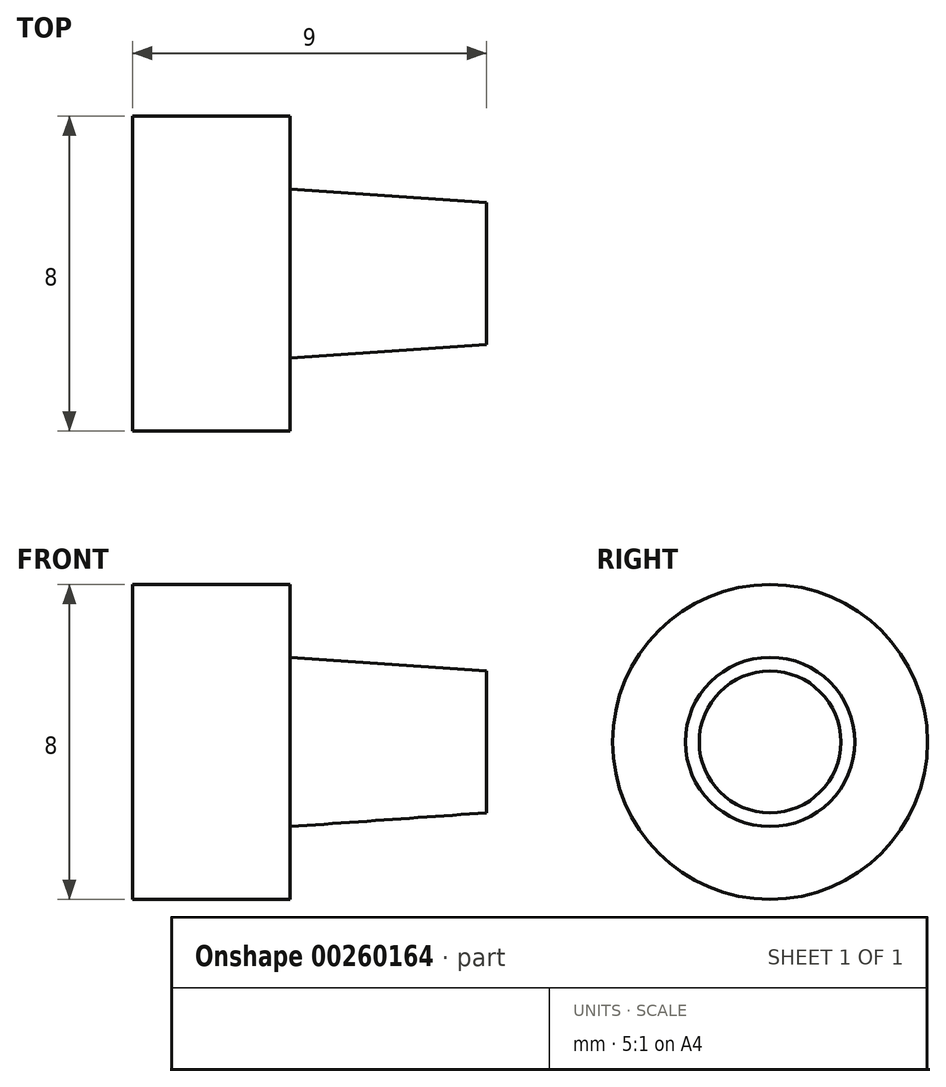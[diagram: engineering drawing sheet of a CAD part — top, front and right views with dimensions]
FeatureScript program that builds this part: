
annotation { "Feature Type Name" : "Feature", "Feature Type Description" : "" }
export const myFeature = defineFeature(function(context is Context, id is Id, definition is map)
    precondition{}
    {
        {
            var Q0;
            Q0=qCreatedBy(makeId("Front.planeOp"),FACE);
            var sketch = newSketch(context, id + "F0", { "sketchPlane" : qUnion([Q0])});
            skLineSegment(sketch, "E0", {"start": v(0, 0) * mm, "end": v(0, 4) * mm});
            skLineSegment(sketch, "E1", {"start": v(0, 4) * mm, "end": v(4, 4) * mm});
            skLineSegment(sketch, "E2", {"start": v(4, 4) * mm, "end": v(4, 2.15) * mm});
            skLineSegment(sketch, "E3", {"start": v(4, 2.15) * mm, "end": v(9, 1.8) * mm});
            skLineSegment(sketch, "E4", {"start": v(9, 1.8) * mm, "end": v(9, 0) * mm});
            skLineSegment(sketch, "E5", {"start": v(9, 0) * mm, "end": v(0, 0) * mm});
            skSolve(sketch);
        }
        {
            var Q0;
            Q0=makeQuery(id+"F0.imprint","IMPRINT",FACE,{"disambiguationData":[TD([[makeQuery(id+"F0.imprint","IMPRINT",EDGE,{"derivedFrom":sQuery(id+"F0.wireOp",EDGE,"E0")}),-1.0]])]});
            var Q1;
            Q1=sQuery(id+"F0.wireOp",EDGE,"E5");
            revolve(context, id + "F1", {"entities" : qUnion([Q0]), "axis" : qUnion([Q1]), "revolveType" : RevolveType.FULL});
        }
    });
